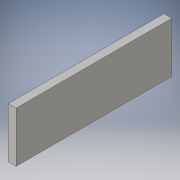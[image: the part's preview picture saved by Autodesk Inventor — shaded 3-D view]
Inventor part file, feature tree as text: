
AUTODESK INVENTOR PART (.ipt)
format: ipt  version: 2016 (Build 200138000, 138)  size: 83,456 bytes
history: native  units: in
note: dims shown in document units (in); Inventor stores cm internally (conversion verified against a paired STEP export)
features: extrude x1, sketch x1
ambient origin geometry x8: Origin, YZ Plane, XZ Plane, XY Plane, X Axis, Y Axis, Z Axis, Center Point
bodies: Solid1 (feature_tree)
feature tree (2):
  extrude  "Extrusion1"  Depth=2.134in
  sketch  "Sketch1"  dims[d0=6.6in d1=2.134in d2=0.335in d3=0.0in]
